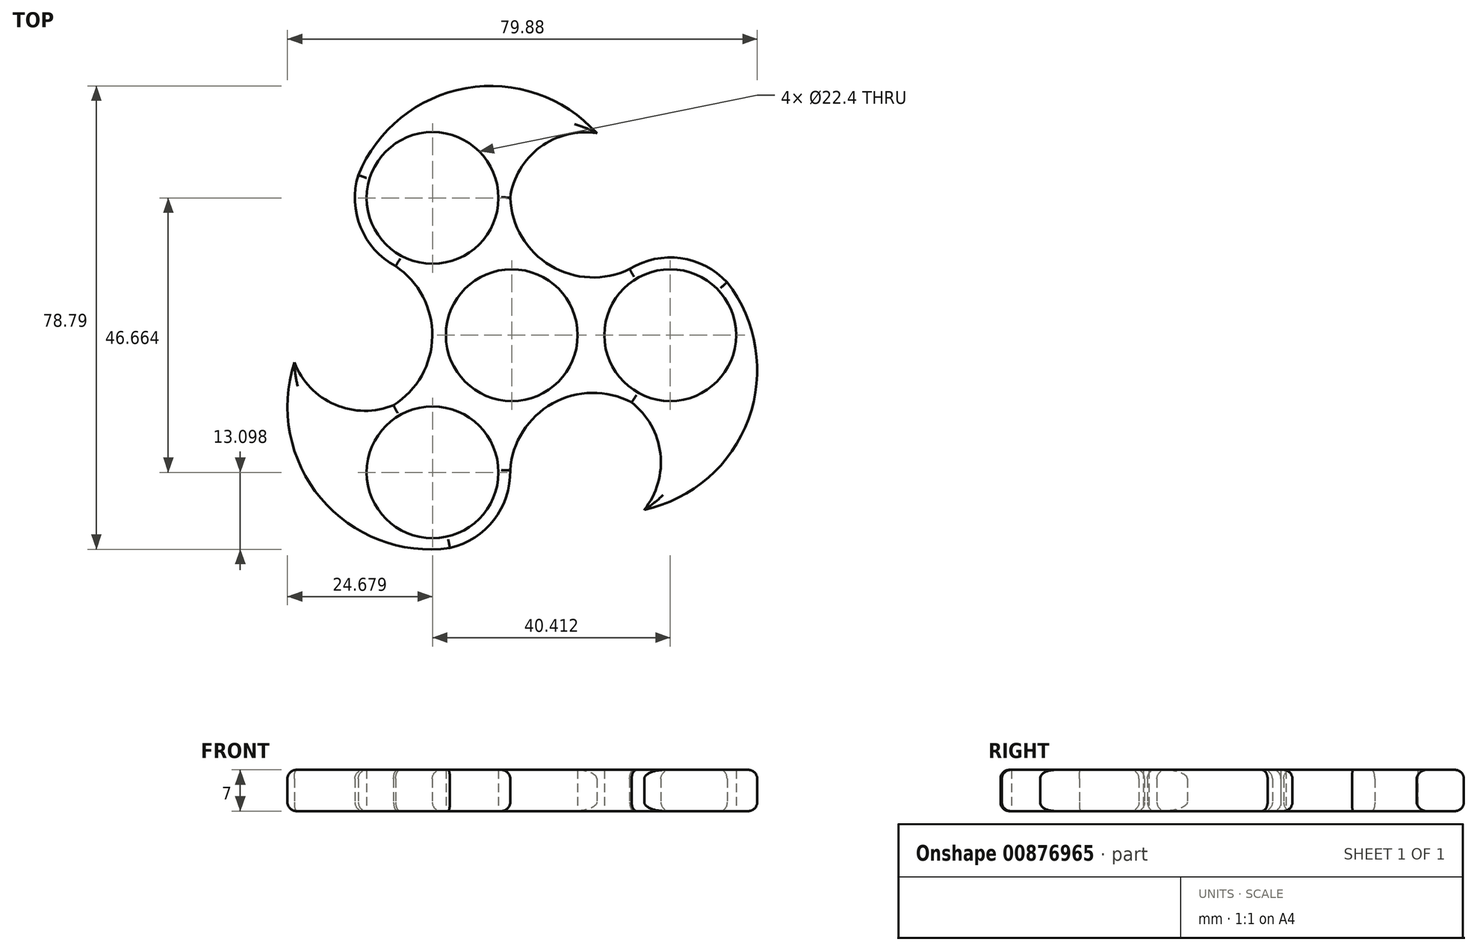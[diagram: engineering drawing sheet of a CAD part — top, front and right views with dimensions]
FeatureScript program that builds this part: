
annotation { "Feature Type Name" : "Feature", "Feature Type Description" : "" }
export const myFeature = defineFeature(function(context is Context, id is Id, definition is map)
    precondition{}
    {
        {
            var Q0;
            Q0=qCreatedBy(makeId("Top.planeOp"),FACE);
            var sketch = newSketch(context, id + "F0", { "sketchPlane" : qUnion([Q0])});
            skCircle(sketch, "E0", {"center": v(0, 0) * mm, "radius": 11.2 * mm});
            skCircle(sketch, "E1", {"center": v(26.94, 0) * mm, "radius": 11.2 * mm});
            skArc(sketch, "E2", {"start": v(39.27, 4.73) * mm, "mid": v(31.18, 12.5) * mm, "end": v(20.03, 11.25) * mm});
            skCircle(sketch, "E3.1.0", {"center": v(-13.47, 23.33) * mm, "radius": 11.2 * mm});
            skArc(sketch, "E3.1.1", {"start": v(-23.73, 31.64) * mm, "mid": v(-26.42, 20.75) * mm, "end": v(-19.76, 11.73) * mm});
            skCircle(sketch, "E3.2.0", {"center": v(-13.47, -23.33) * mm, "radius": 11.2 * mm});
            skArc(sketch, "E3.2.1", {"start": v(-15.54, -36.37) * mm, "mid": v(-4.76, -33.25) * mm, "end": v(-0.28, -22.97) * mm});
            skArc(sketch, "E4", {"start": v(-20.1, -11.92) * mm, "mid": v(-13.52, -0.19) * mm, "end": v(-19.76, 11.73) * mm});
            skArc(sketch, "E5.1.0", {"start": v(20.37, -11.45) * mm, "mid": v(6.92, -11.61) * mm, "end": v(-0.28, -22.97) * mm});
            skArc(sketch, "E5.2.0", {"start": v(-0.27, 23.37) * mm, "mid": v(6.6, 11.8) * mm, "end": v(20.03, 11.25) * mm});
            skArc(sketch, "E6", {"start": v(-36.97, -4.66) * mm, "mid": v(-30.06, -11.82) * mm, "end": v(-20.1, -11.92) * mm});
            skArc(sketch, "E7", {"start": v(-36.97, -4.66) * mm, "mid": v(-32.47, -27.74) * mm, "end": v(-10.52, -36.2) * mm});
            skArc(sketch, "E8.1.0", {"start": v(22.52, -29.69) * mm, "mid": v(25.26, -20.12) * mm, "end": v(20.37, -11.45) * mm});
            skArc(sketch, "E8.2.0", {"start": v(14.45, 34.35) * mm, "mid": v(4.8, 31.94) * mm, "end": v(-0.27, 23.37) * mm});
            skArc(sketch, "E9.1.0", {"start": v(22.52, -29.69) * mm, "mid": v(40.26, -14.25) * mm, "end": v(36.61, 8.99) * mm});
            skArc(sketch, "E9.2.0", {"start": v(14.45, 34.35) * mm, "mid": v(-7.8, 41.99) * mm, "end": v(-26.09, 27.21) * mm});
            skSolve(sketch);
        }
        {
            var Q0;
            Q0=makeQuery(id+"F0.imprint","IMPRINT",FACE,{"disambiguationData":[TD([[makeQuery(id+"F0.imprint","IMPRINT",EDGE,{"derivedFrom":sQuery(id+"F0.wireOp",EDGE,"E0")}),-1.0]])]});
            extrude(context, id + "F1", {"entities" : qUnion([Q0]), "depth" : 7 * mm, "offsetDistance" : 25 * mm});
        }
        {
            var Q0;
            Q0=makeQuery(id+"F1.opExtrude","CAP_EDGE",EDGE,{"disambiguationData":[OSD([sQuery(id+"F0.wireOp",EDGE,"E5.1.0")])],"isStart":false});
            var Q1;
            Q1=makeQuery(id+"F1.opExtrude","CAP_EDGE",EDGE,{"disambiguationData":[OSD([sQuery(id+"F0.wireOp",EDGE,"E3.2.1")])],"isStart":false});
            var Q2;
            Q2=makeQuery(id+"F1.opExtrude","CAP_EDGE",EDGE,{"disambiguationData":[OSD([sQuery(id+"F0.wireOp",EDGE,"E7")])],"isStart":false});
            var Q3;
            Q3=makeQuery(id+"F1.opExtrude","CAP_EDGE",EDGE,{"disambiguationData":[OSD([sQuery(id+"F0.wireOp",EDGE,"E6")])],"isStart":false});
            var Q4;
            Q4=makeQuery(id+"F1.opExtrude","CAP_EDGE",EDGE,{"disambiguationData":[OSD([sQuery(id+"F0.wireOp",EDGE,"E4")])],"isStart":false});
            var Q5;
            Q5=makeQuery(id+"F1.opExtrude","CAP_EDGE",EDGE,{"disambiguationData":[OSD([sQuery(id+"F0.wireOp",EDGE,"E3.1.1")])],"isStart":false});
            var Q6;
            Q6=makeQuery(id+"F1.opExtrude","CAP_EDGE",EDGE,{"disambiguationData":[OSD([sQuery(id+"F0.wireOp",EDGE,"E9.2.0")])],"isStart":false});
            var Q7;
            Q7=makeQuery(id+"F1.opExtrude","CAP_EDGE",EDGE,{"disambiguationData":[OSD([sQuery(id+"F0.wireOp",EDGE,"E8.2.0")])],"isStart":false});
            var Q8;
            Q8=makeQuery(id+"F1.opExtrude","CAP_EDGE",EDGE,{"disambiguationData":[OSD([sQuery(id+"F0.wireOp",EDGE,"E5.2.0")])],"isStart":false});
            var Q9;
            Q9=makeQuery(id+"F1.opExtrude","CAP_EDGE",EDGE,{"disambiguationData":[OSD([sQuery(id+"F0.wireOp",EDGE,"E2")])],"isStart":false});
            var Q10;
            Q10=makeQuery(id+"F1.opExtrude","CAP_EDGE",EDGE,{"disambiguationData":[OSD([sQuery(id+"F0.wireOp",EDGE,"E9.1.0")])],"isStart":false});
            var Q11;
            Q11=makeQuery(id+"F1.opExtrude","CAP_EDGE",EDGE,{"disambiguationData":[OSD([sQuery(id+"F0.wireOp",EDGE,"E8.1.0")])],"isStart":false});
            fillet(context, id + "F2", {"entities" : qUnion([Q0, Q1, Q2, Q3, Q4, Q5, Q6, Q7, Q8, Q9, Q10, Q11]), "radius" : 1.5 * mm, "tangentPropagation" : true, "allowEdgeOverflow" : false});
        }
        {
            var Q0;
            Q0=makeQuery(id+"F1.opExtrude","CAP_EDGE",EDGE,{"disambiguationData":[OSD([sQuery(id+"F0.wireOp",EDGE,"E4")])],"isStart":true});
            var Q1;
            Q1=makeQuery(id+"F1.opExtrude","CAP_EDGE",EDGE,{"disambiguationData":[OSD([sQuery(id+"F0.wireOp",EDGE,"E3.1.1")])],"isStart":true});
            var Q2;
            Q2=makeQuery(id+"F1.opExtrude","CAP_EDGE",EDGE,{"disambiguationData":[OSD([sQuery(id+"F0.wireOp",EDGE,"E9.2.0")])],"isStart":true});
            var Q3;
            Q3=makeQuery(id+"F1.opExtrude","CAP_EDGE",EDGE,{"disambiguationData":[OSD([sQuery(id+"F0.wireOp",EDGE,"E8.2.0")])],"isStart":true});
            var Q4;
            Q4=makeQuery(id+"F1.opExtrude","CAP_EDGE",EDGE,{"disambiguationData":[OSD([sQuery(id+"F0.wireOp",EDGE,"E5.2.0")])],"isStart":true});
            var Q5;
            Q5=makeQuery(id+"F1.opExtrude","CAP_EDGE",EDGE,{"disambiguationData":[OSD([sQuery(id+"F0.wireOp",EDGE,"E2")])],"isStart":true});
            var Q6;
            Q6=makeQuery(id+"F1.opExtrude","CAP_EDGE",EDGE,{"disambiguationData":[OSD([sQuery(id+"F0.wireOp",EDGE,"E9.1.0")])],"isStart":true});
            var Q7;
            Q7=makeQuery(id+"F1.opExtrude","CAP_EDGE",EDGE,{"disambiguationData":[OSD([sQuery(id+"F0.wireOp",EDGE,"E8.1.0")])],"isStart":true});
            var Q8;
            Q8=makeQuery(id+"F1.opExtrude","CAP_EDGE",EDGE,{"disambiguationData":[OSD([sQuery(id+"F0.wireOp",EDGE,"E5.1.0")])],"isStart":true});
            var Q9;
            Q9=makeQuery(id+"F1.opExtrude","CAP_EDGE",EDGE,{"disambiguationData":[OSD([sQuery(id+"F0.wireOp",EDGE,"E3.2.1")])],"isStart":true});
            var Q10;
            Q10=makeQuery(id+"F1.opExtrude","CAP_EDGE",EDGE,{"disambiguationData":[OSD([sQuery(id+"F0.wireOp",EDGE,"E7")])],"isStart":true});
            var Q11;
            Q11=makeQuery(id+"F1.opExtrude","CAP_EDGE",EDGE,{"disambiguationData":[OSD([sQuery(id+"F0.wireOp",EDGE,"E6")])],"isStart":true});
            fillet(context, id + "F3", {"entities" : qUnion([Q0, Q1, Q2, Q3, Q4, Q5, Q6, Q7, Q8, Q9, Q10, Q11]), "radius" : 1.5 * mm, "tangentPropagation" : true, "allowEdgeOverflow" : false});
        }
    });
